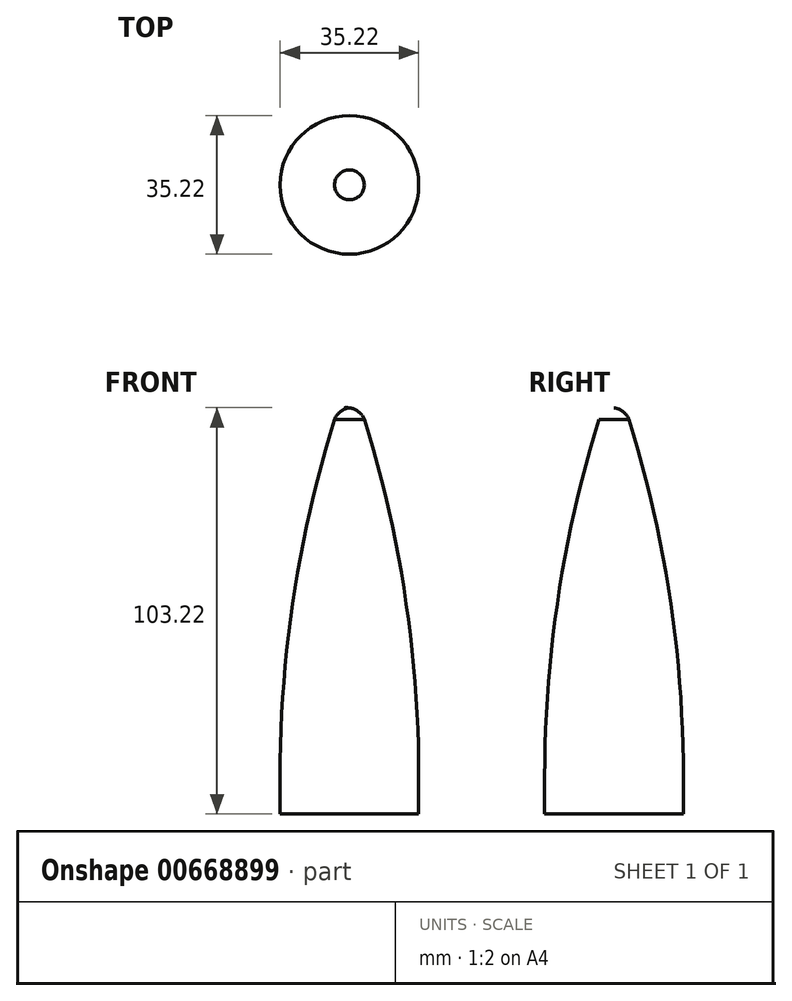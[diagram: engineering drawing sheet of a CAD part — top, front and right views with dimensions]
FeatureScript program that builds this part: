
annotation { "Feature Type Name" : "Feature", "Feature Type Description" : "" }
export const myFeature = defineFeature(function(context is Context, id is Id, definition is map)
    precondition{}
    {
        {
            var Q0;
            Q0=qCreatedBy(makeId("Front.planeOp"),FACE);
            var sketch = newSketch(context, id + "F0", { "sketchPlane" : qUnion([Q0])});
            skLineSegment(sketch, "E0", {"start": v(13.65, 0) * mm, "end": v(14.3, 0) * mm});
            skLineSegment(sketch, "E1", {"start": v(0, 0) * mm, "end": v(0, 111.13) * mm});
            skPoint(sketch, "E2.end.orphan", {"position": v(0, 9.53) * mm});
            skLineSegment(sketch, "E3", {"start": v(17.46, 0) * mm, "end": v(14.3, 0) * mm});
            skLineSegment(sketch, "E4", {"start": v(0, 0) * mm, "end": v(0, 53.9) * mm});
            skLineSegment(sketch, "E5", {"start": v(17.46, 9.53) * mm, "end": v(18.73, 9.53) * mm});
            skLineSegment(sketch, "E6", {"start": v(0, 111.13) * mm, "end": v(0, 112.4) * mm});
            skArc(sketch, "E7", {"start": v(1.2, 111.55) * mm, "mid": v(0.69, 112.1) * mm, "end": v(0, 112.4) * mm});
            skLineSegment(sketch, "E8", {"start": v(0, 99.07) * mm, "end": v(0, 100.34) * mm});
            skLineSegment(sketch, "E9", {"start": v(0, 100.34) * mm, "end": v(0, 101.9) * mm});
            skLineSegment(sketch, "E10", {"start": v(0, 0) * mm, "end": v(17.48, 0) * mm});
            skLineSegment(sketch, "E11.0", {"start": v(17.6, 9.53) * mm, "end": v(17.6, 0) * mm});
            skArc(sketch, "E11.1", {"start": v(17.6, 9.53) * mm, "mid": v(14.13, 55.39) * mm, "end": v(3.78, 100.2) * mm});
            skLineSegment(sketch, "E12", {"start": v(0, 101.9) * mm, "end": v(0, 103.18) * mm});
            skArc(sketch, "E13", {"start": v(3.78, 100.2) * mm, "mid": v(2.3, 102.2) * mm, "end": v(0, 103.18) * mm});
            skLineSegment(sketch, "E14", {"start": v(17.48, 0) * mm, "end": v(15.19, 0) * mm});
            skLineSegment(sketch, "E15", {"start": v(15.19, 0) * mm, "end": v(15.19, 9.53) * mm});
            skPoint(sketch, "E16.endSnap0", {"position": v(1.5, 101.2) * mm});
            skLineSegment(sketch, "E17", {"start": v(1.5, 100.2) * mm, "end": v(0, 101.12) * mm});
            skArc(sketch, "E18", {"start": v(15.19, 9.53) * mm, "mid": v(11.75, 55.38) * mm, "end": v(1.5, 100.2) * mm});
            skLineSegment(sketch, "E19", {"start": v(17.6, 0) * mm, "end": v(15.19, 0) * mm});
            skSolve(sketch);
        }
        {
            var Q0;
            Q0 = qSketchRegion(id + "F0", true);
            var Q1;
            Q1=sQuery(id+"F0.wireOp",EDGE,"E1");
            revolve(context, id + "F1", {"entities" : qUnion([Q0]), "axis" : qUnion([Q1]), "revolveType" : RevolveType.FULL});
        }
    });
